# Revit family: pascala_round_901557_002_2_730_52ac
name_source: partatom
category: Lighting Fixtures
units: mm (PartAtom-declared; Revit-internal decimal feet)

## family parameters
Cut with Voids When Loaded = No
Host = Face
Light Source = No
Part Type = Normal
Room Calculation Point = No
Round Connector Dimension = Use Diameter
Shared = No

## types (1)
- TuneableWhite 846 (1 x LED Modul 846, 2900 lm, 4600)
    Apparent Load = 30 VA
    CIE Flux Codes = 94 99 100 100 100
    Color Rendering = 80
    Color Temperature = 4600
    Default Elevation = 1800 mm
    Description = Series: PASCALA round
High quality recessed downlight. Mounting bracket: galvanised sheet steel. Inner and closure ring: die-cast aluminium. Brilliantly luminous corona at the light-emitting surfaces thanks to use of a specially designed cast aluminium ring as a reflector closure. Reflector material: MIRO-SILVER with 98 percent total light reflection. Patented round design shaped like a truncated cone. Tunable white dynamically adjustable from 2700 K to 6500 K. Installation without tools thanks to spring fastening system. Converter in separate ballast box with connecting cable plugged in. With connecting cable (L 400 mm). Through-wiring box (5 pole) available as accessory. Possible accessories - please order separately: Extensive selection of accessory covers - can all be retrofitted without tools. IP 54 to be achieved with corresponding accessories. 
Colour: traffic white, matt (RAL 9016)
Diameter: 241 mm
Height: 2 mm
Cut-out diameter: 228 mm
Recess height: 160 mm
Luminaire: recess height: 156 mm
Lamp: LED
Socket: without socket
Colour temperature: 2700K - 6500K
Colour rendering index (CRI): 80
System power: 30 W
Rated luminous flux: 2900 lm
Luminous efficiency: 97 lm/W
System power 2: 31 W
Rated luminous flux 2: 2800 lm
Luminous efficiency 2: 90 lm/W
System power 3: 30 W
Rated luminous flux 3: 2650 lm
Luminous efficiency 3: 88 lm/W
Control gear: Dimmable Bluetooth converter
Protection class: II
Type of protection: IP 20
    Height = 0 mm  [stored 0 ft]
    Lamp = 1 x LED Modul 846
    Lamp Light Flux = 2900 lm
    Lamp count = 1
    Length = 241 mm
    Lifetime = 50000 h
    Luminous efficacy = 97 lm/W
    Manufacturer = RZB
    ModVariant = No
    Model = 901557.002.2.730
    Mounting Place = Ceiling
    Mounting Type = Recessed
    Number of Poles = 1
    OnlyDefault = Yes
    Power Factor = 1
    Product Name = PASCALA round
    Product group = Recessed downlights
    ProductGroupID = 402
    Protection Class = Protection class II
    Protection Degree = IP 20
    RLX_Detail_Level = 1
    RLX_Emergency_Light_Flux = 0 lm
    RLX_Emergency_Type = 0
    RLX_Emergency_Type_DB = No
    RlxData = <blob elided: 47885 chars, md5=21b52e98>
    Socket = socket
    Standby Power = 0 W
    System Light Flux = 2900 lm
    System Power = 30 W
    Type Comments = TuneableWhite 846
    Type Image = 901557.002.jpg
    URL = http://relux.com
    VarID = tuneablewhite_846
    Voltage = 230 V
    Voltage Range = 220-240 V
    Weight = 0.00 kg
    Width = 0 mm  [stored 0 ft]

note: [stored X ft] marks values corroborated as IEEE doubles in the binary element streams (Revit-internal decimal feet)

## geometry (parser evidence)
native form markers: Sweep x11
no freeform markers — native parametric forms only
